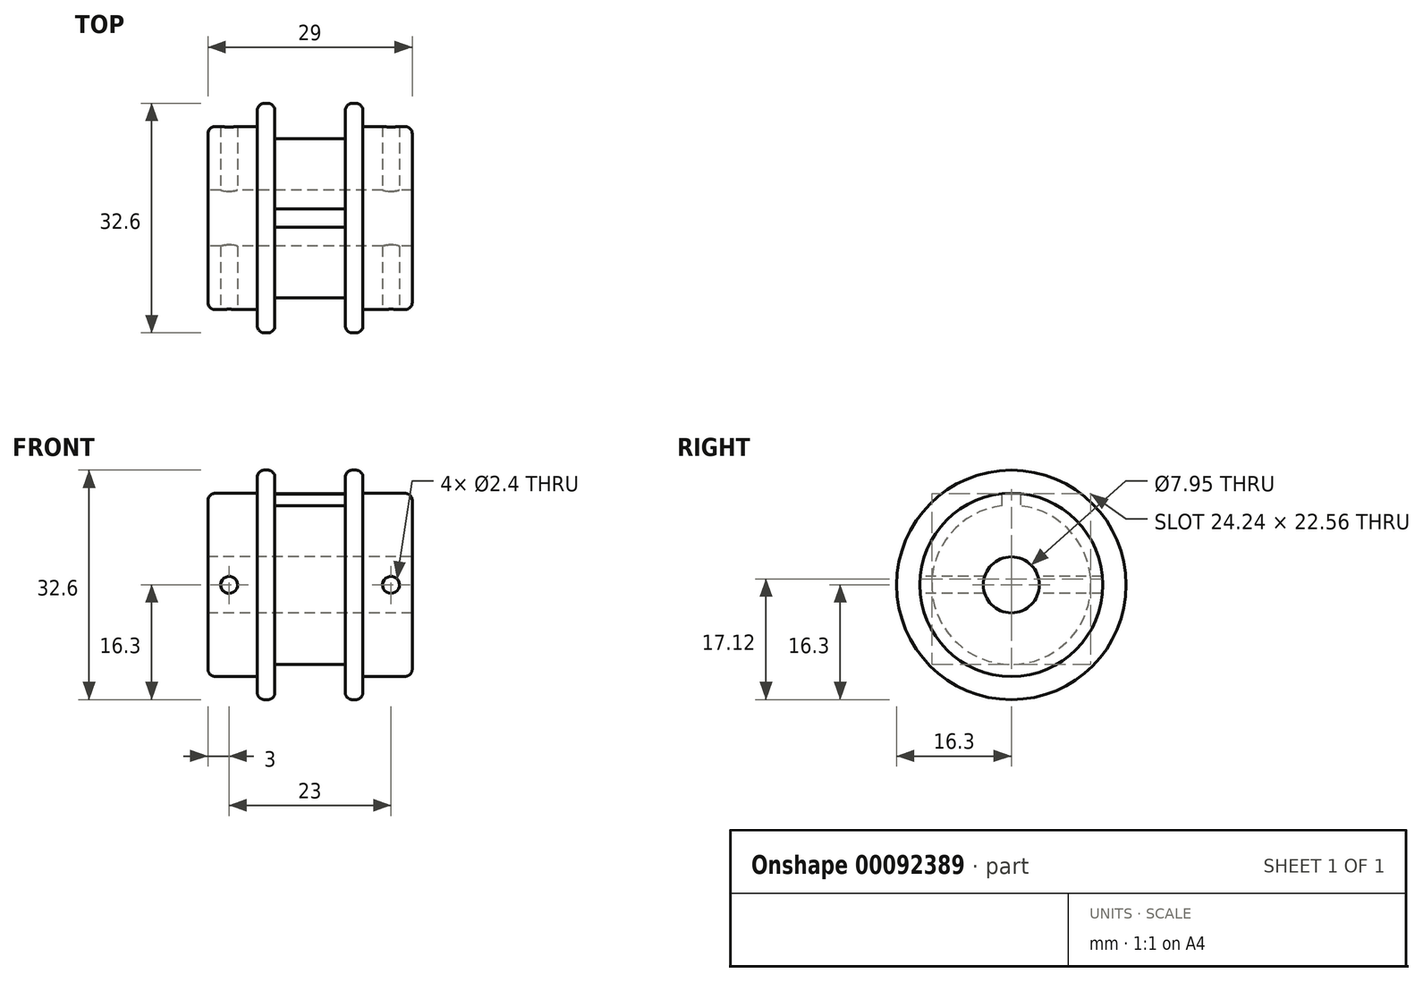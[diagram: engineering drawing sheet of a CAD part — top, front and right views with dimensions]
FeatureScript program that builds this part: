
annotation { "Feature Type Name" : "Feature", "Feature Type Description" : "" }
export const myFeature = defineFeature(function(context is Context, id is Id, definition is map)
    precondition{}
    {
        {
            var Q0;
            Q0=qCreatedBy(makeId("Right.planeOp"),FACE);
            var sketch = newSketch(context, id + "F0", { "sketchPlane" : qUnion([Q0])});
            skCircle(sketch, "E0", {"center": v(0, 0) * mm, "radius": 3.98 * mm});
            skCircle(sketch, "E1", {"center": v(0, 0) * mm, "radius": 13 * mm});
            skSolve(sketch);
        }
        {
            var Q0;
            Q0=makeQuery(id+"F0.imprint","IMPRINT",FACE,{"disambiguationData":[TD([[makeQuery(id+"F0.imprint","IMPRINT",EDGE,{"derivedFrom":sQuery(id+"F0.wireOp",EDGE,"E0")}),-1.0]])]});
            extrude(context, id + "F1", {"entities" : qUnion([Q0]), "endBound" : BoundingType.SYMMETRIC, "depth" : 29 * mm});
        }
        {
            var Q0;
            Q0=qCreatedBy(makeId("Front.planeOp"),FACE);
            var sketch = newSketch(context, id + "F2", { "sketchPlane" : qUnion([Q0])});
            skLineSegment(sketch, "E2", {"start": v(-27.37, 0) * mm, "end": v(29.66, 0) * mm});
            skLineSegment(sketch, "E3.bottom", {"start": v(-7.5, 16.3) * mm, "end": v(7.5, 16.3) * mm});
            skLineSegment(sketch, "E3.top", {"start": v(-7.5, 11.3) * mm, "end": v(7.5, 11.3) * mm});
            skLineSegment(sketch, "E3.left", {"start": v(-7.5, 16.3) * mm, "end": v(-7.5, 11.3) * mm});
            skLineSegment(sketch, "E3.right", {"start": v(7.5, 16.3) * mm, "end": v(7.5, 11.3) * mm});
            skLineSegment(sketch, "E4", {"start": v(-5, 16.3) * mm, "end": v(-5, 11.3) * mm});
            skLineSegment(sketch, "E5", {"start": v(5, 16.3) * mm, "end": v(5, 11.3) * mm});
            skSolve(sketch);
        }
        {
            var Q0;
            {var subQ0=sQuery(id+"F2.wireOp",EDGE,"E3.left");Q0=makeQuery(id+"F2.imprint","IMPRINT",FACE,{"disambiguationData":[TD([[makeQuery(id+"F2.imprint","IMPRINT",EDGE,{"derivedFrom":subQ0}),1.0]])]});}
            var Q1;
            {var subQ0=sQuery(id+"F2.wireOp",EDGE,"E3.right");Q1=makeQuery(id+"F2.imprint","IMPRINT",FACE,{"disambiguationData":[TD([[makeQuery(id+"F2.imprint","IMPRINT",EDGE,{"derivedFrom":subQ0}),-1.0]])]});}
            var Q2;
            Q2=sQuery(id+"F2.wireOp",EDGE,"E2");
            revolve(context, id + "F3", {"operationType" : NewBodyOperationType.ADD, "entities" : qUnion([Q0, Q1]), "axis" : qUnion([Q2]), "revolveType" : RevolveType.FULL});
        }
        {
            var Q0;
            Q0=qCreatedBy(makeId("Front.planeOp"),FACE);
            var sketch = newSketch(context, id + "F4", { "sketchPlane" : qUnion([Q0])});
            skCircle(sketch, "E6", {"center": v(-11.5, 0) * mm, "radius": 1.2 * mm});
            skCircle(sketch, "E7", {"center": v(11.5, 0) * mm, "radius": 1.2 * mm});
            skSolve(sketch);
        }
        {
            var Q0;
            Q0=makeQuery(id+"F4.imprint","IMPRINT",FACE,{"disambiguationData":[TD([[makeQuery(id+"F4.imprint","IMPRINT",EDGE,{"derivedFrom":sQuery(id+"F4.wireOp",EDGE,"E6")}),1.0]])]});
            var Q1;
            Q1=makeQuery(id+"F4.imprint","IMPRINT",FACE,{"disambiguationData":[TD([[makeQuery(id+"F4.imprint","IMPRINT",EDGE,{"derivedFrom":sQuery(id+"F4.wireOp",EDGE,"E7")}),1.0]])]});
            extrude(context, id + "F5", {"entities" : qUnion([Q0, Q1]), "operationType" : NewBodyOperationType.REMOVE, "endBound" : BoundingType.SYMMETRIC, "oppositeDirection" : true, "depth" : 30 * mm});
        }
        {
            var Q0;
            {var subQ0=sQuery(id+"F2.wireOp",EDGE,"E4");Q0=makeQuery(id+"F2.imprint","IMPRINT",FACE,{"disambiguationData":[TD([[makeQuery(id+"F2.imprint","IMPRINT",EDGE,{"derivedFrom":subQ0}),1.0]])]});}
            var Q1;
            Q1=sQuery(id+"F2.wireOp",EDGE,"E2");
            revolve(context, id + "F6", {"operationType" : NewBodyOperationType.REMOVE, "entities" : qUnion([Q0]), "axis" : qUnion([Q1]), "revolveType" : RevolveType.FULL, "oppositeDirection" : true});
        }
        {
            var Q0;
            {var subQ0=sQuery(id+"F2.wireOp",EDGE,"E4");Q0=makeQuery(id+"F6.boolean.opBoolean","MERGE",FACE,{"derivedFrom":[makeQuery(id+"F3.opRevolve","SWEPT_FACE",FACE,{"disambiguationData":[OSD([subQ0])]}),makeQuery(id+"F6.opRevolve","SWEPT_FACE",FACE,{"disambiguationData":[OSD([subQ0])]})]});}
            var sketch = newSketch(context, id + "F7", { "sketchPlane" : qUnion([Q0])});
            skArc(sketch, "E8", {"start": v(-1.3, 11.17) * mm, "mid": v(0, -11.25) * mm, "end": v(1.3, 11.17) * mm, "construction": true});
            skArc(sketch, "E9", {"start": v(1.3, 11.17) * mm, "mid": v(0, 11.25) * mm, "end": v(-1.3, 11.17) * mm});
            skPoint(sketch, "E10.visualSharp", {"position": v(-1.3, 12.87) * mm});
            skPoint(sketch, "E11.visualSharp", {"position": v(1.3, 12.87) * mm});
            skArc(sketch, "E12", {"start": v(-0.65, 12.92) * mm, "mid": v(0, -12.94) * mm, "end": v(0.65, 12.92) * mm});
            skArc(sketch, "E13", {"start": v(0.65, 12.92) * mm, "mid": v(-0.2, 12.94) * mm, "end": v(-1.04, 12.9) * mm});
            skLineSegment(sketch, "E14", {"start": v(-1.3, 11.17) * mm, "end": v(-1.3, 12.87) * mm});
            skLineSegment(sketch, "E15", {"start": v(1.3, 12.87) * mm, "end": v(1.3, 11.17) * mm});
            skSolve(sketch);
        }
        {
            var Q0;
            {var subQ0=sQuery(id+"F7.wireOp",EDGE,"E13");var subQ3=makeQuery(id+"F7.imprint","IMPRINT",VERTEX,{"derivedFrom":subQ0});Q0=makeQuery(id+"F7.imprint","IMPRINT",FACE,{"disambiguationData":[TD([[makeQuery(id+"F7.imprint","IMPRINT",EDGE,{"disambiguationData":[TD([[subQ3,1.0]])],"derivedFrom":subQ0}),1.0]])]});}
            extrude(context, id + "F8", {"entities" : qUnion([Q0]), "operationType" : NewBodyOperationType.ADD, "depth" : 10 * mm});
        }
        {
            var Q0;
            Q0=makeQuery(id+"F3.opRevolve","SWEPT_EDGE",EDGE,{"disambiguationData":[OSD([sQuery(id+"F2.wireOp",EDGE,"E3.bottom"),sQuery(id+"F2.wireOp",EDGE,"E4")])]});
            var Q1;
            Q1=makeQuery(id+"F3.opRevolve","SWEPT_EDGE",EDGE,{"disambiguationData":[OSD([sQuery(id+"F2.wireOp",EDGE,"E3.bottom"),sQuery(id+"F2.wireOp",EDGE,"E5")])]});
            var Q2;
            Q2=makeQuery(id+"F1.opExtrude","CAP_EDGE",EDGE,{"disambiguationData":[OSD([sQuery(id+"F0.wireOp",EDGE,"E1")])],"isStart":true});
            var Q3;
            Q3=makeQuery(id+"F1.opExtrude","CAP_EDGE",EDGE,{"disambiguationData":[OSD([sQuery(id+"F0.wireOp",EDGE,"E1")])],"isStart":false});
            var Q4;
            Q4=makeQuery(id+"F3.opRevolve","SWEPT_EDGE",EDGE,{"disambiguationData":[OSD([sQuery(id+"F2.wireOp",EDGE,"E3.bottom"),sQuery(id+"F2.wireOp",EDGE,"E3.left")])]});
            var Q5;
            Q5=makeQuery(id+"F3.opRevolve","SWEPT_EDGE",EDGE,{"disambiguationData":[OSD([sQuery(id+"F2.wireOp",EDGE,"E3.bottom"),sQuery(id+"F2.wireOp",EDGE,"E3.right")])]});
            fillet(context, id + "F9", {"entities" : qUnion([Q0, Q1, Q2, Q3, Q4, Q5]), "radius" : 1 * mm, "tangentPropagation" : true, "allowEdgeOverflow" : false});
        }
    });
